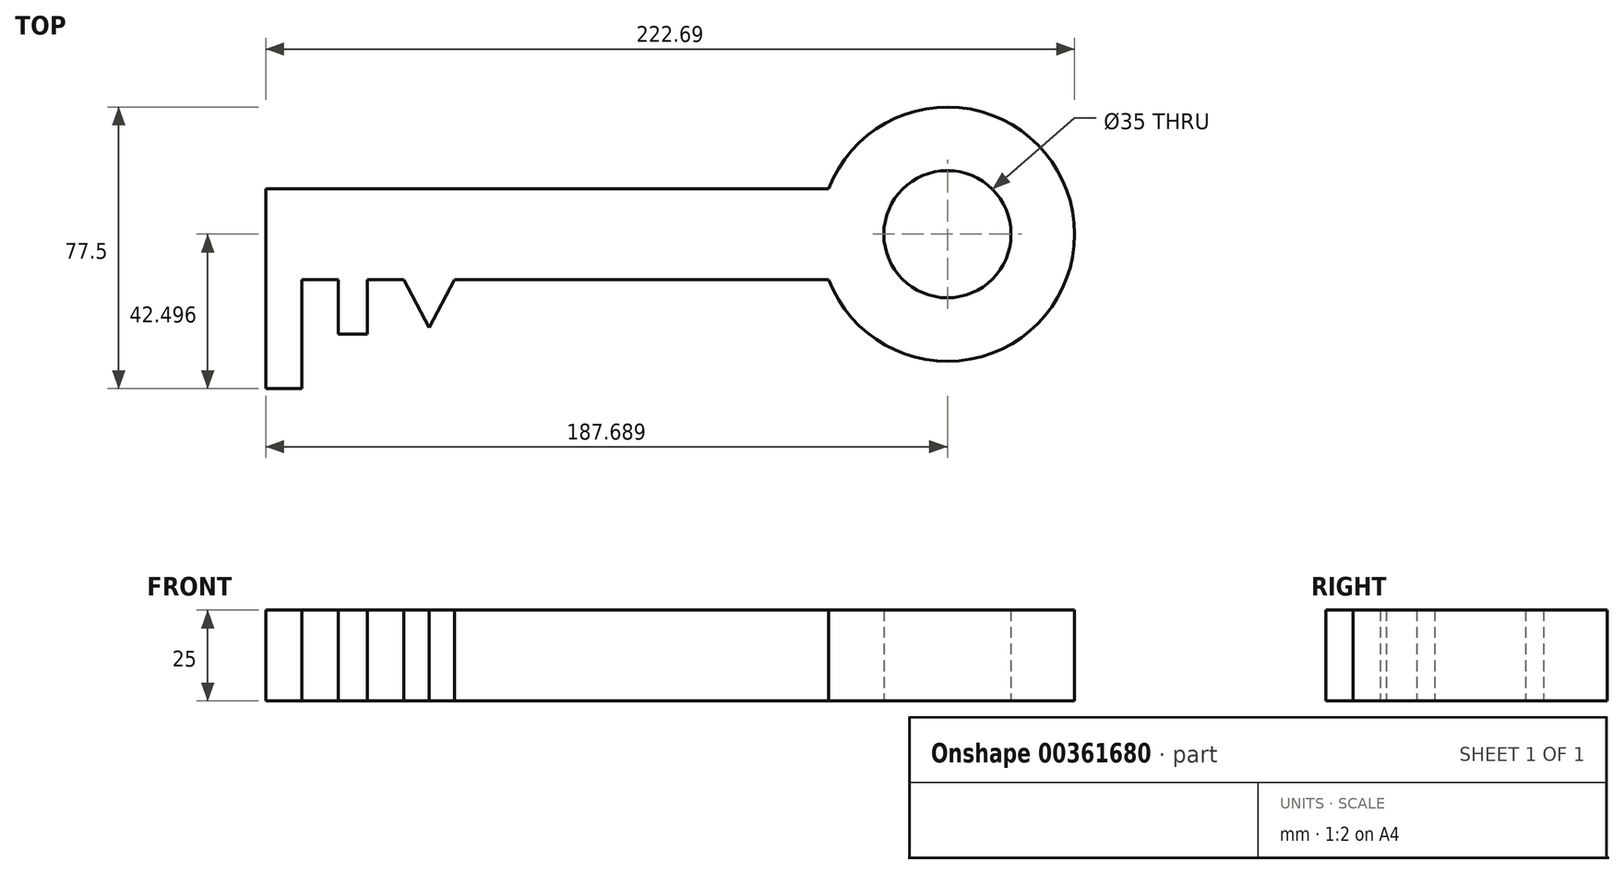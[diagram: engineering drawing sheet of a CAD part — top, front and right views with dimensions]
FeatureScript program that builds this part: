
annotation { "Feature Type Name" : "Feature", "Feature Type Description" : "" }
export const myFeature = defineFeature(function(context is Context, id is Id, definition is map)
    precondition{}
    {
        {
            var Q0;
            Q0=qCreatedBy(makeId("Top.planeOp"),FACE);
            var sketch = newSketch(context, id + "F0", { "sketchPlane" : qUnion([Q0])});
            skLineSegment(sketch, "E0.bottom", {"start": v(-119.06, 38.27) * mm, "end": v(35.94, 38.27) * mm});
            skLineSegment(sketch, "E0.top", {"start": v(-109.06, 13.27) * mm, "end": v(-99.06, 13.27) * mm});
            skLineSegment(sketch, "E0.left", {"start": v(-119.06, 38.27) * mm, "end": v(-119.06, 13.27) * mm});
            skLineSegment(sketch, "E1.top", {"start": v(-119.06, -16.73) * mm, "end": v(-109.06, -16.73) * mm});
            skLineSegment(sketch, "E1.left", {"start": v(-119.06, 13.27) * mm, "end": v(-119.06, -16.73) * mm});
            skLineSegment(sketch, "E1.right", {"start": v(-109.06, 13.27) * mm, "end": v(-109.06, -16.73) * mm});
            skLineSegment(sketch, "E2.top", {"start": v(-99.06, -1.73) * mm, "end": v(-91.06, -1.73) * mm});
            skLineSegment(sketch, "E2.left", {"start": v(-99.06, 13.27) * mm, "end": v(-99.06, -1.73) * mm});
            skLineSegment(sketch, "E2.right", {"start": v(-91.06, 13.27) * mm, "end": v(-91.06, -1.73) * mm});
            skLineSegment(sketch, "E3", {"start": v(-81.06, 13.27) * mm, "end": v(-74.06, 0) * mm});
            skLineSegment(sketch, "E4", {"start": v(-74.06, 0) * mm, "end": v(-67.06, 13.27) * mm});
            skLineSegment(sketch, "E5", {"start": v(-91.06, 13.27) * mm, "end": v(-81.06, 13.27) * mm});
            skArc(sketch, "E6", {"start": v(35.94, 13.27) * mm, "mid": v(103.63, 25.77) * mm, "end": v(35.94, 38.27) * mm});
            skCircle(sketch, "E7", {"center": v(68.63, 25.77) * mm, "radius": 17.5 * mm});
            skLineSegment(sketch, "E8.trimOffspring", {"start": v(-67.06, 13.27) * mm, "end": v(35.94, 13.27) * mm});
            skSolve(sketch);
        }
        {
            var Q0;
            Q0 = qSketchRegion(id + "F0", true);
            extrude(context, id + "F1", {"entities" : qUnion([Q0]), "depth" : 25 * mm});
        }
    });
